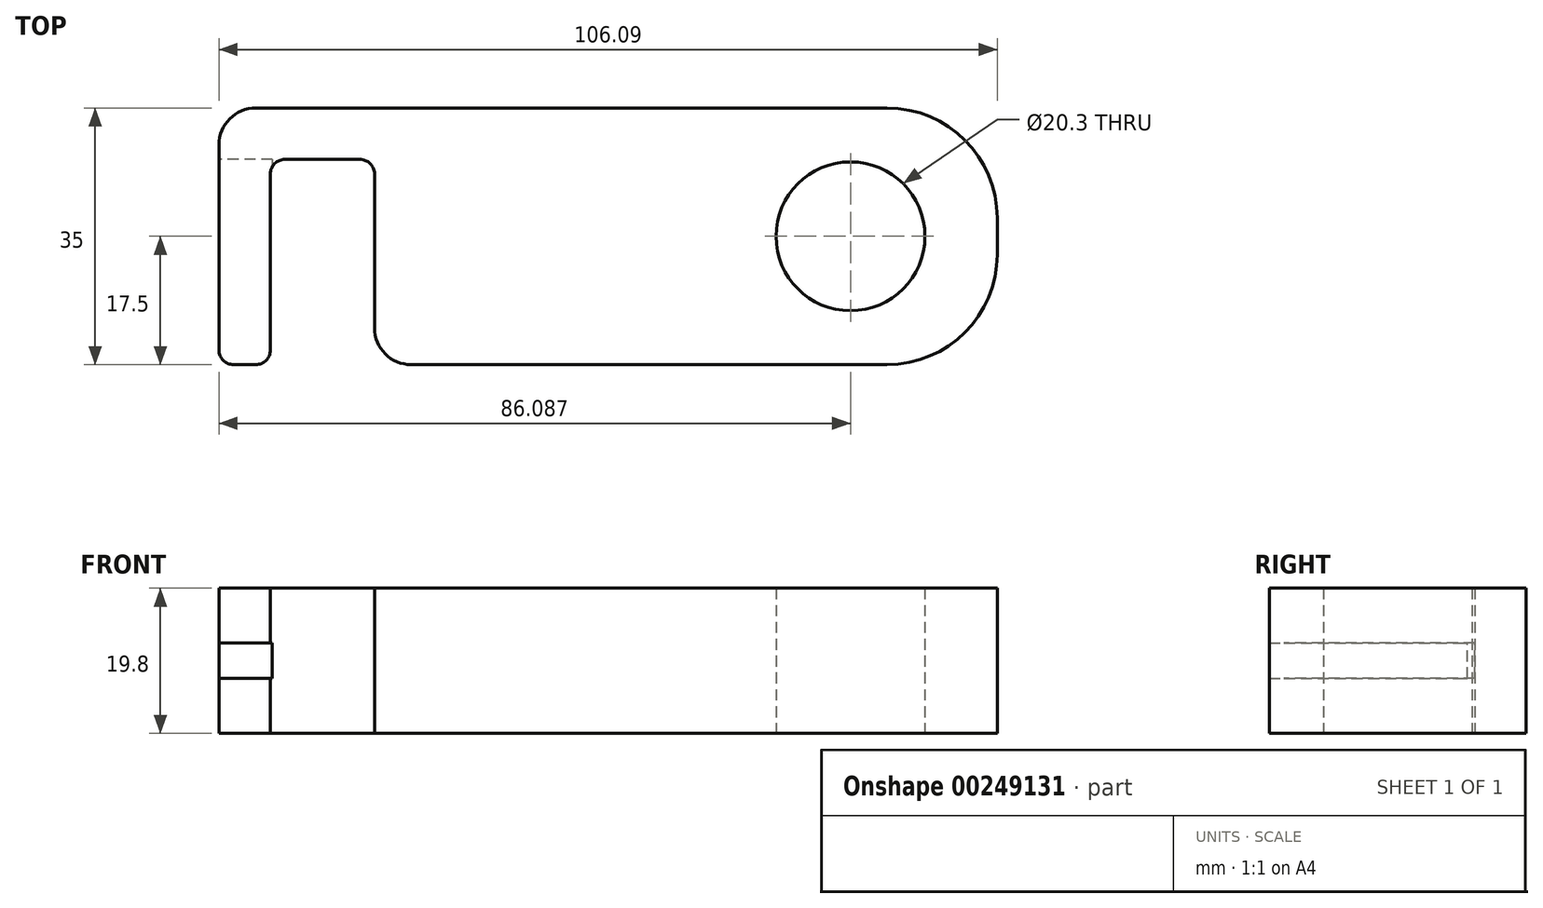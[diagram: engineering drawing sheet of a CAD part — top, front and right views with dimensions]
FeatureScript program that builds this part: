
annotation { "Feature Type Name" : "Feature", "Feature Type Description" : "" }
export const myFeature = defineFeature(function(context is Context, id is Id, definition is map)
    precondition{}
    {
        {
            var Q0;
            Q0=qCreatedBy(makeId("Top.planeOp"),FACE);
            var sketch = newSketch(context, id + "F0", { "sketchPlane" : qUnion([Q0])});
            skLineSegment(sketch, "E0", {"start": v(-56.2, -17.5) * mm, "end": v(-56.2, 17.5) * mm});
            skLineSegment(sketch, "E1", {"start": v(-56.2, 17.5) * mm, "end": v(49.89, 17.5) * mm});
            skLineSegment(sketch, "E2", {"start": v(49.89, 17.5) * mm, "end": v(49.89, -17.5) * mm});
            skLineSegment(sketch, "E3", {"start": v(49.89, -17.5) * mm, "end": v(-35, -17.5) * mm});
            skLineSegment(sketch, "E4", {"start": v(-35, -17.5) * mm, "end": v(-35, 10.5) * mm});
            skLineSegment(sketch, "E5", {"start": v(-35, 10.5) * mm, "end": v(-49.2, 10.5) * mm});
            skLineSegment(sketch, "E6", {"start": v(-49.2, 10.5) * mm, "end": v(-49.2, -17.5) * mm});
            skLineSegment(sketch, "E7", {"start": v(-49.2, -17.5) * mm, "end": v(-56.2, -17.5) * mm});
            skCircle(sketch, "E8", {"center": v(29.89, 0) * mm, "radius": 10.15 * mm});
            skSolve(sketch);
        }
        {
            var Q0;
            Q0=makeQuery(id+"F0.imprint","IMPRINT",FACE,{"disambiguationData":[TD([[makeQuery(id+"F0.imprint","IMPRINT",EDGE,{"derivedFrom":sQuery(id+"F0.wireOp",EDGE,"E0")}),-1.0]])]});
            extrude(context, id + "F1", {"entities" : qUnion([Q0]), "depth" : 19.8 * mm});
        }
        {
            var Q0;
            Q0=makeQuery(id+"F1.opExtrude","SWEPT_EDGE",EDGE,{"disambiguationData":[OSD([sQuery(id+"F0.wireOp",EDGE,"E1"),sQuery(id+"F0.wireOp",EDGE,"E2")])]});
            var Q1;
            Q1=makeQuery(id+"F1.opExtrude","SWEPT_EDGE",EDGE,{"disambiguationData":[OSD([sQuery(id+"F0.wireOp",EDGE,"E2"),sQuery(id+"F0.wireOp",EDGE,"E3")])]});
            fillet(context, id + "F2", {"entities" : qUnion([Q0, Q1]), "radius" : 15 * mm, "tangentPropagation" : true, "allowEdgeOverflow" : false});
        }
        {
            var Q0;
            Q0=makeQuery(id+"F1.opExtrude","SWEPT_EDGE",EDGE,{"disambiguationData":[OSD([sQuery(id+"F0.wireOp",EDGE,"E3"),sQuery(id+"F0.wireOp",EDGE,"E4")])]});
            fillet(context, id + "F3", {"entities" : qUnion([Q0]), "radius" : 5 * mm, "tangentPropagation" : true, "allowEdgeOverflow" : false});
        }
        {
            var Q0;
            Q0=makeQuery(id+"F1.opExtrude","SWEPT_EDGE",EDGE,{"disambiguationData":[OSD([sQuery(id+"F0.wireOp",EDGE,"E0"),sQuery(id+"F0.wireOp",EDGE,"E1")])]});
            fillet(context, id + "F4", {"entities" : qUnion([Q0]), "radius" : 5 * mm, "tangentPropagation" : true, "allowEdgeOverflow" : false});
        }
        {
            var Q0;
            Q0=makeQuery(id+"F1.opExtrude","SWEPT_EDGE",EDGE,{"disambiguationData":[OSD([sQuery(id+"F0.wireOp",EDGE,"E6"),sQuery(id+"F0.wireOp",EDGE,"E7")])]});
            var Q1;
            Q1=makeQuery(id+"F1.opExtrude","SWEPT_EDGE",EDGE,{"disambiguationData":[OSD([sQuery(id+"F0.wireOp",EDGE,"E0"),sQuery(id+"F0.wireOp",EDGE,"E7")])]});
            fillet(context, id + "F5", {"entities" : qUnion([Q0, Q1]), "radius" : 2 * mm, "tangentPropagation" : true, "allowEdgeOverflow" : false});
        }
        {
            var Q0;
            Q0=makeQuery(id+"F1.opExtrude","SWEPT_EDGE",EDGE,{"disambiguationData":[OSD([sQuery(id+"F0.wireOp",EDGE,"E5"),sQuery(id+"F0.wireOp",EDGE,"E6")])]});
            var Q1;
            Q1=makeQuery(id+"F1.opExtrude","SWEPT_EDGE",EDGE,{"disambiguationData":[OSD([sQuery(id+"F0.wireOp",EDGE,"E4"),sQuery(id+"F0.wireOp",EDGE,"E5")])]});
            fillet(context, id + "F6", {"entities" : qUnion([Q0, Q1]), "radius" : 2 * mm, "tangentPropagation" : true, "allowEdgeOverflow" : false});
        }
        {
            var Q0;
            Q0=makeQuery(id+"F1.opExtrude","SWEPT_FACE",FACE,{"disambiguationData":[OSD([sQuery(id+"F0.wireOp",EDGE,"E7")])]});
            var sketch = newSketch(context, id + "F7", { "sketchPlane" : qUnion([Q0])});
            skLineSegment(sketch, "E9", {"start": v(-56.69, 9.9) * mm, "end": v(-48.92, 9.9) * mm});
            skPoint(sketch, "E9.startSnap0", {"position": v(-51.2, 9.9) * mm});
            skLineSegment(sketch, "E10.bottom", {"start": v(-56.69, 7.5) * mm, "end": v(-48.92, 7.5) * mm});
            skLineSegment(sketch, "E10.top", {"start": v(-56.69, 12.3) * mm, "end": v(-48.92, 12.3) * mm});
            skLineSegment(sketch, "E10.left", {"start": v(-56.69, 7.5) * mm, "end": v(-56.69, 12.3) * mm});
            skLineSegment(sketch, "E10.right", {"start": v(-48.92, 7.5) * mm, "end": v(-48.92, 12.3) * mm});
            skSolve(sketch);
        }
        {
            var Q0;
            Q0=qSketchRegion(id+"F7",true);
            var Q1;
            Q1=makeQuery(id+"F1.opExtrude","SWEPT_FACE",FACE,{"disambiguationData":[OSD([sQuery(id+"F0.wireOp",EDGE,"E5")])]});
            var Q2;
            Q2=makeQuery(id+"F1.opExtrude","SWEPT_BODY",BODY,{"disambiguationData":[OSD([sQuery(id+"F0.wireOp",EDGE,"E0"),sQuery(id+"F0.wireOp",EDGE,"E1"),sQuery(id+"F0.wireOp",EDGE,"E2"),sQuery(id+"F0.wireOp",EDGE,"E3"),sQuery(id+"F0.wireOp",EDGE,"E4"),sQuery(id+"F0.wireOp",EDGE,"E5"),sQuery(id+"F0.wireOp",EDGE,"E6"),sQuery(id+"F0.wireOp",EDGE,"E7"),sQuery(id+"F0.wireOp",EDGE,"E8"),sQuery(id+"F0.wireOp",EDGE,"tit84n2c-8nMz-OdRq-PZTD-TIhe18ebcCe5")])]});
            extrude(context, id + "F8", {"entities" : qUnion([Q0]), "operationType" : NewBodyOperationType.REMOVE, "endBound" : BoundingType.UP_TO_SURFACE, "oppositeDirection" : true, "endBoundEntityFace" : qUnion([Q1]), "endBoundEntityBody" : qUnion([Q2]), "depth" : 25 * mm});
        }
    });
